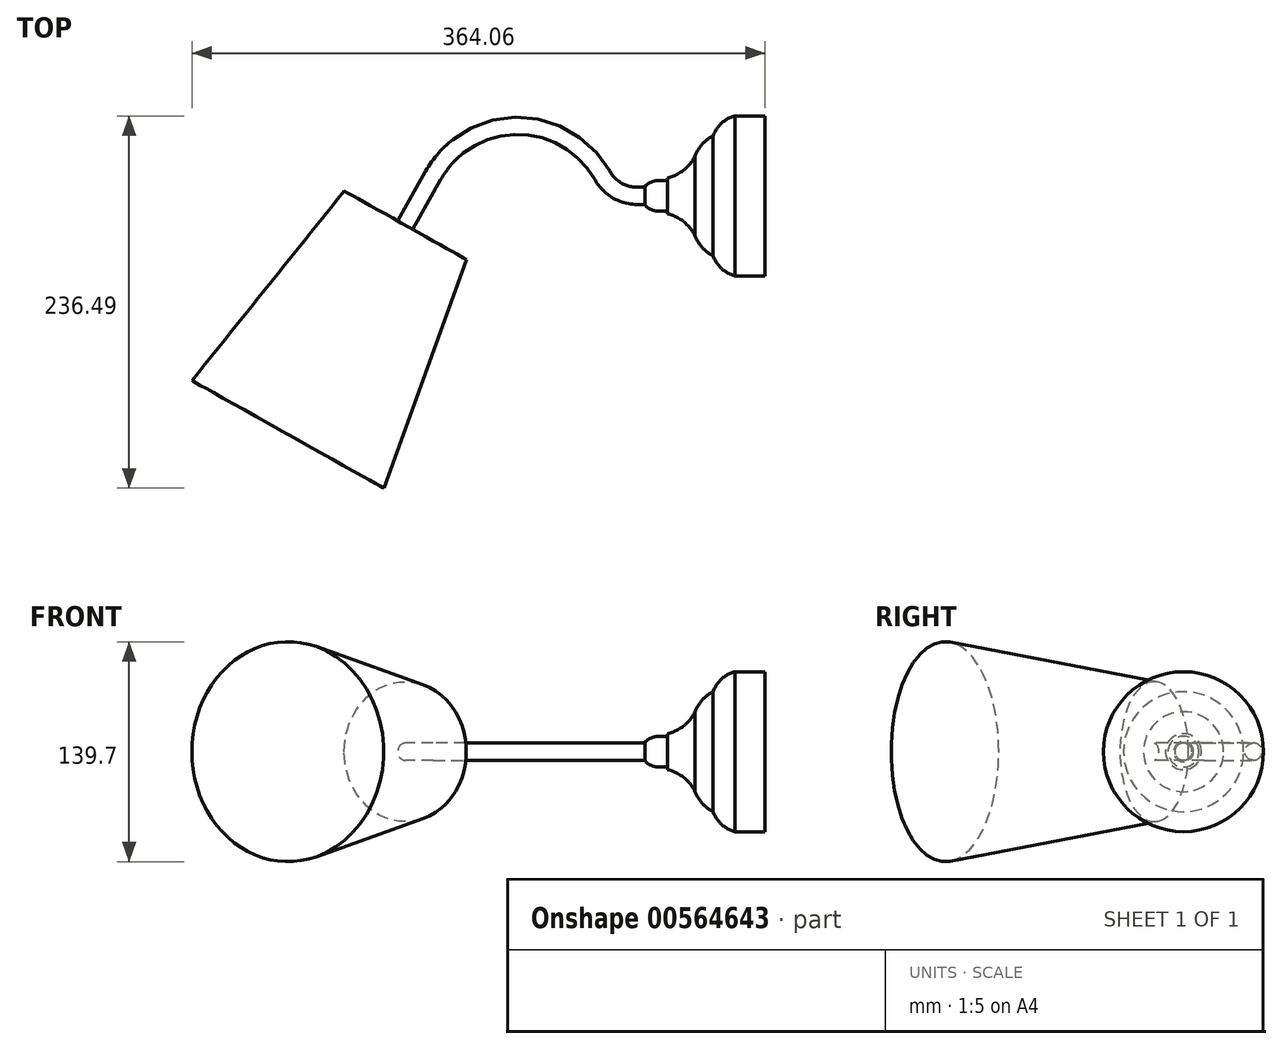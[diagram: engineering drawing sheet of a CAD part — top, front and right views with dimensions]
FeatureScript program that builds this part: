
annotation { "Feature Type Name" : "Feature", "Feature Type Description" : "" }
export const myFeature = defineFeature(function(context is Context, id is Id, definition is map)
    precondition{}
    {
        {
            var Q0;
            Q0=qCreatedBy(makeId("Top.planeOp"),FACE);
            var sketch = newSketch(context, id + "F0", { "sketchPlane" : qUnion([Q0])});
            skLineSegment(sketch, "E0", {"start": v(0, 0) * mm, "end": v(-76.2, 0) * mm});
            skLineSegment(sketch, "E1", {"start": v(0, 0) * mm, "end": v(0, 50.8) * mm});
            skLineSegment(sketch, "E2", {"start": v(0, 50.8) * mm, "end": v(-19.05, 50.8) * mm});
            skArc(sketch, "E3", {"start": v(-19.05, 50.8) * mm, "mid": v(-27.65, 46.22) * mm, "end": v(-33.02, 38.1) * mm});
            skArc(sketch, "E4", {"start": v(-33.02, 38.1) * mm, "mid": v(-39.95, 32.85) * mm, "end": v(-44.45, 25.4) * mm});
            skArc(sketch, "E5", {"start": v(-62.18, 11.43) * mm, "mid": v(-51.75, 16.43) * mm, "end": v(-44.45, 25.4) * mm});
            skLineSegment(sketch, "E6", {"start": v(-62.18, 11.43) * mm, "end": v(-62.18, 9.8) * mm});
            skLineSegment(sketch, "E7", {"start": v(-62.18, 9.8) * mm, "end": v(-66.9, 9.8) * mm});
            skArc(sketch, "E8", {"start": v(-66.9, 9.8) * mm, "mid": v(-71.86, 8.9) * mm, "end": v(-76.2, 6.35) * mm});
            skLineSegment(sketch, "E9", {"start": v(-76.2, 0) * mm, "end": v(-76.2, 6.35) * mm});
            skSolve(sketch);
        }
        {
            var Q0;
            Q0=makeQuery(id+"F0.imprint","IMPRINT",FACE,{"disambiguationData":[TD([[makeQuery(id+"F0.imprint","IMPRINT",EDGE,{"derivedFrom":sQuery(id+"F0.wireOp",EDGE,"E0")}),-1.0]])]});
            var Q1;
            Q1=sQuery(id+"F0.wireOp",EDGE,"E0");
            revolve(context, id + "F1", {"entities" : qUnion([Q0]), "axis" : qUnion([Q1]), "revolveType" : RevolveType.FULL});
        }
        {
            var Q0;
            Q0=qCreatedBy(makeId("Top.planeOp"),FACE);
            var sketch = newSketch(context, id + "F2", { "sketchPlane" : qUnion([Q0])});
            skLineSegment(sketch, "E10", {"start": v(-76.2, 0) * mm, "end": v(-81.28, 0) * mm});
            skArc(sketch, "E11", {"start": v(-103.43, 12.98) * mm, "mid": v(-94.12, 3.48) * mm, "end": v(-81.28, 0) * mm});
            skArc(sketch, "E12", {"start": v(-103.43, 12.98) * mm, "mid": v(-157.16, 44.45) * mm, "end": v(-210.9, 12.98) * mm});
            skLineSegment(sketch, "E13", {"start": v(-210.9, 12.98) * mm, "end": v(-228.6, -18.6) * mm});
            skLineSegment(sketch, "E14", {"start": v(-157.16, 44.45) * mm, "end": v(-233.69, 44.45) * mm, "construction": true});
            skPoint(sketch, "E14.endSnap0", {"position": v(-157.16, 44.45) * mm});
            skSolve(sketch);
        }
        {
            var Q0;
            Q0=makeQuery(id+"F1.opRevolve","SWEPT_FACE",FACE,{"disambiguationData":[OSD([sQuery(id+"F0.wireOp",EDGE,"E9")])]});
            var sketch = newSketch(context, id + "F3", { "sketchPlane" : qUnion([Q0])});
            skCircle(sketch, "E15", {"center": v(0, 0) * mm, "radius": 5.45 * mm});
            skSolve(sketch);
        }
        {
            var Q0;
            Q0=qSketchRegion(id+"F3",true);
            var Q1;
            Q1=qConstructionFilter(qBodyType(qCreatedBy(id+"F2",EDGE),BodyType.WIRE),ConstructionObject.NO);
            sweep(context, id + "F4", {"operationType" : NewBodyOperationType.ADD, "profiles" : qUnion([Q0]), "path" : qUnion([Q1])});
        }
        {
            var Q0;
            Q0=qCreatedBy(makeId("Top.planeOp"),FACE);
            var sketch = newSketch(context, id + "F5", { "sketchPlane" : qUnion([Q0])});
            skLineSegment(sketch, "E16", {"start": v(-223.85, -21.27) * mm, "end": v(-206.14, 10.31) * mm, "construction": true});
            skLineSegment(sketch, "E17", {"start": v(-215.65, 15.64) * mm, "end": v(-233.35, -15.94) * mm, "construction": true});
            skLineSegment(sketch, "E18", {"start": v(-233.35, -15.94) * mm, "end": v(-223.85, -21.27) * mm, "construction": true});
            skLineSegment(sketch, "E19", {"start": v(-228.6, -18.6) * mm, "end": v(-303.13, -151.53) * mm});
            skLineSegment(sketch, "E20", {"start": v(-228.6, -18.6) * mm, "end": v(-189.83, -40.34) * mm});
            skLineSegment(sketch, "E21", {"start": v(-303.13, -151.53) * mm, "end": v(-242.2, -185.7) * mm});
            skLineSegment(sketch, "E22", {"start": v(-242.2, -185.7) * mm, "end": v(-189.83, -40.34) * mm});
            skSolve(sketch);
        }
        {
            var Q0;
            Q0=makeQuery(id+"F5.imprint","IMPRINT",FACE,{"disambiguationData":[TD([[makeQuery(id+"F5.imprint","IMPRINT",EDGE,{"derivedFrom":sQuery(id+"F5.wireOp",EDGE,"E19")}),1.0]])]});
            var Q1;
            Q1=sQuery(id+"F5.wireOp",EDGE,"E19");
            revolve(context, id + "F6", {"operationType" : NewBodyOperationType.ADD, "entities" : qUnion([Q0]), "axis" : qUnion([Q1]), "revolveType" : RevolveType.FULL});
        }
    });
